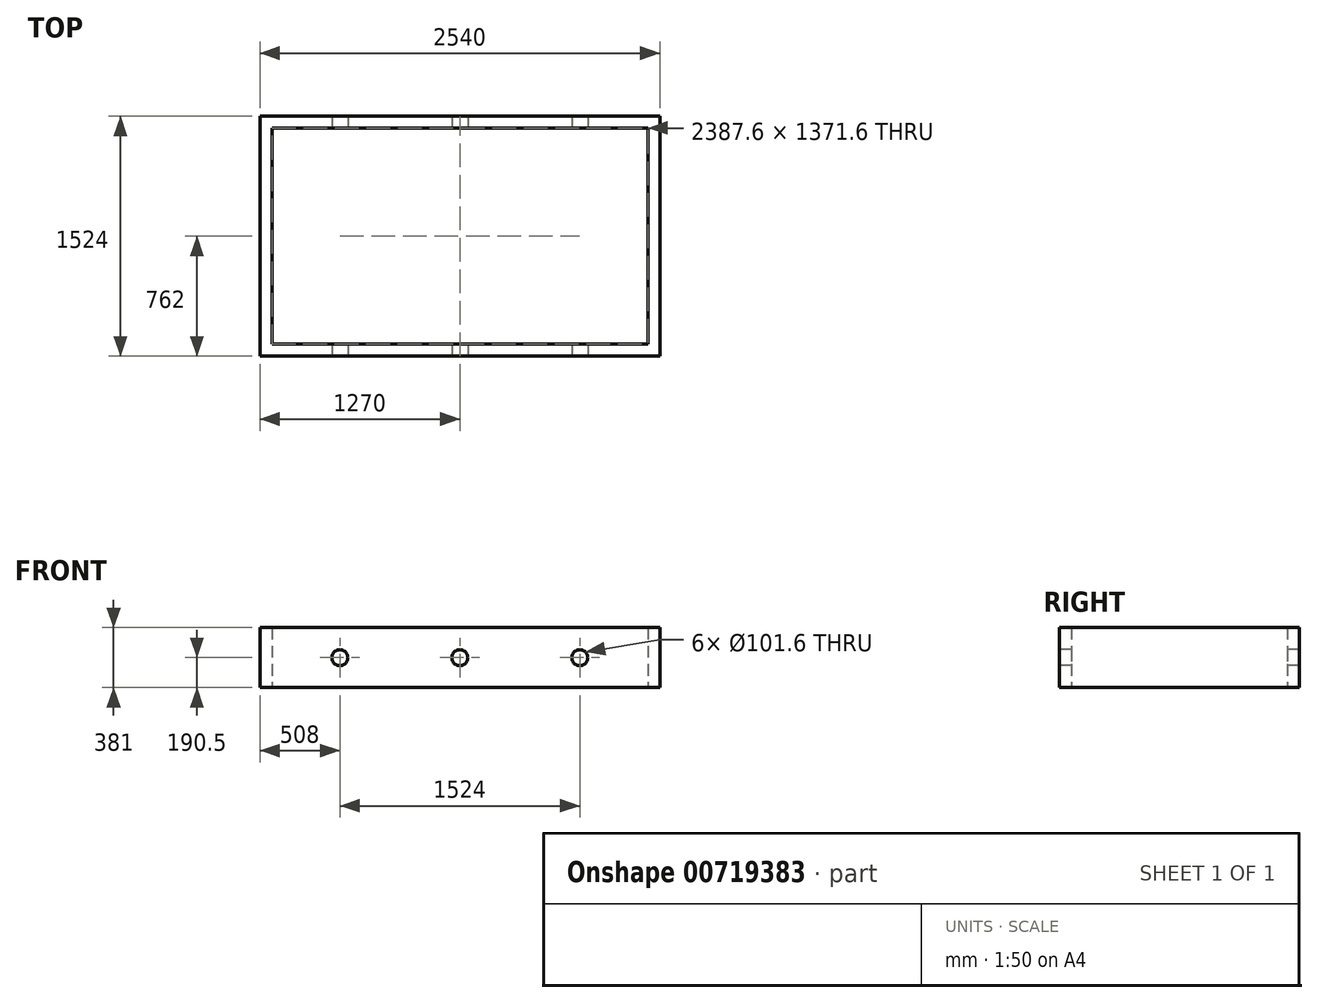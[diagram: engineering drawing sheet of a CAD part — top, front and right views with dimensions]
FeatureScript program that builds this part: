
annotation { "Feature Type Name" : "Feature", "Feature Type Description" : "" }
export const myFeature = defineFeature(function(context is Context, id is Id, definition is map)
    precondition{}
    {
        {
            var Q0;
            Q0=qCreatedBy(makeId("Top.planeOp"),FACE);
            var sketch = newSketch(context, id + "F0", { "sketchPlane" : qUnion([Q0])});
            skLineSegment(sketch, "E0.bottom", {"start": v(-1270, 762) * mm, "end": v(1270, 762) * mm});
            skLineSegment(sketch, "E0.top", {"start": v(-1270, -762) * mm, "end": v(1270, -762) * mm});
            skLineSegment(sketch, "E0.left", {"start": v(-1270, 762) * mm, "end": v(-1270, -762) * mm});
            skLineSegment(sketch, "E0.right", {"start": v(1270, 762) * mm, "end": v(1270, -762) * mm});
            skLineSegment(sketch, "E1.bottom", {"start": v(-1193.8, 685.8) * mm, "end": v(1193.8, 685.8) * mm});
            skLineSegment(sketch, "E1.top", {"start": v(-1193.8, -685.8) * mm, "end": v(1193.8, -685.8) * mm});
            skLineSegment(sketch, "E1.left", {"start": v(-1193.8, 685.8) * mm, "end": v(-1193.8, -685.8) * mm});
            skLineSegment(sketch, "E1.right", {"start": v(1193.8, 685.8) * mm, "end": v(1193.8, -685.8) * mm});
            skSolve(sketch);
        }
        {
            var Q0;
            Q0 = qSketchRegion(id + "F0", true);
            extrude(context, id + "F1", {"entities" : qUnion([Q0]), "depth" : 381 * mm, "offsetDistance" : 25.4 * mm});
        }
        {
            var Q0;
            Q0=makeQuery(id+"F1.opExtrude","SWEPT_FACE",FACE,{"disambiguationData":[OSD([sQuery(id+"F0.wireOp",EDGE,"E0.top")])]});
            var sketch = newSketch(context, id + "F2", { "sketchPlane" : qUnion([Q0])});
            skCircle(sketch, "E2", {"center": v(-762, 190.5) * mm, "radius": 50.8 * mm});
            skCircle(sketch, "E3", {"center": v(762, 190.5) * mm, "radius": 50.8 * mm});
            skCircle(sketch, "E4", {"center": v(0, 190.5) * mm, "radius": 50.8 * mm});
            skSolve(sketch);
        }
        {
            var Q0;
            Q0 = qSketchRegion(id + "F2", true);
            extrude(context, id + "F3", {"entities" : qUnion([Q0]), "operationType" : NewBodyOperationType.REMOVE, "endBound" : BoundingType.THROUGH_ALL, "oppositeDirection" : true, "depth" : 25.4 * mm, "offsetDistance" : 25.4 * mm});
        }
    });
